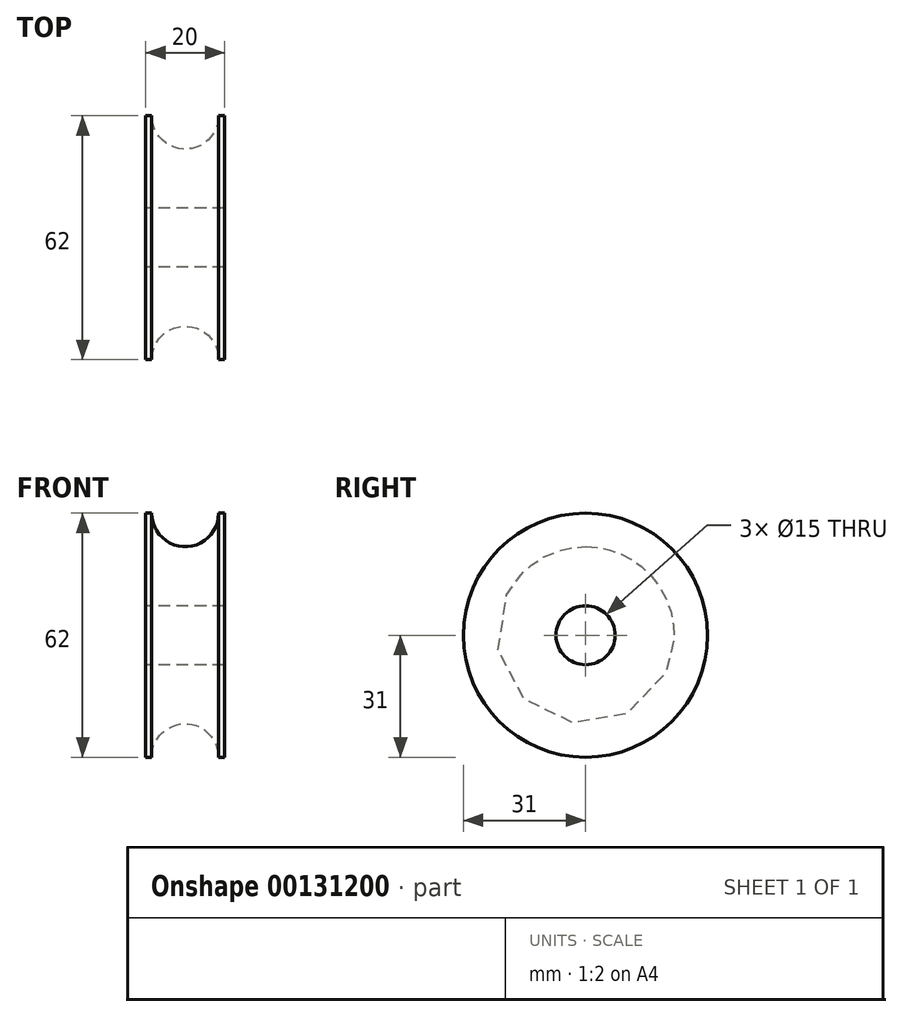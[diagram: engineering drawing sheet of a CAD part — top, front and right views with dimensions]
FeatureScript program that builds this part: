
annotation { "Feature Type Name" : "Feature", "Feature Type Description" : "" }
export const myFeature = defineFeature(function(context is Context, id is Id, definition is map)
    precondition{}
    {
        {
            var Q0;
            Q0=qCreatedBy(makeId("Front.planeOp"),FACE);
            var sketch = newSketch(context, id + "F0", { "sketchPlane" : qUnion([Q0])});
            skLineSegment(sketch, "E0", {"start": v(0, 0) * mm, "end": v(29.21, 0) * mm});
            skLineSegment(sketch, "E1", {"start": v(-10, 7.5) * mm, "end": v(10, 7.5) * mm});
            skLineSegment(sketch, "E2", {"start": v(10, 7.5) * mm, "end": v(10, 31) * mm});
            skLineSegment(sketch, "E3", {"start": v(10, 31) * mm, "end": v(8.5, 31) * mm});
            skLineSegment(sketch, "E4", {"start": v(-10, 31) * mm, "end": v(-10, 7.5) * mm});
            skLineSegment(sketch, "E5", {"start": v(0, 0) * mm, "end": v(0, 7.5) * mm});
            skArc(sketch, "E6", {"start": v(-8.5, 31) * mm, "mid": v(0, 22.5) * mm, "end": v(8.5, 31) * mm});
            skLineSegment(sketch, "E7.trimOffspring", {"start": v(-8.5, 31) * mm, "end": v(-10, 31) * mm});
            skSolve(sketch);
        }
        {
            var Q0;
            {var subQ0=sQuery(id+"F0.wireOp",EDGE,"E2");Q0=makeQuery(id+"F0.imprint","IMPRINT",FACE,{"disambiguationData":[TD([[makeQuery(id+"F0.imprint","IMPRINT",EDGE,{"derivedFrom":subQ0}),1.0]])]});}
            var Q1;
            Q1=sQuery(id+"F0.wireOp",EDGE,"E0");
            revolve(context, id + "F1", {"entities" : qUnion([Q0]), "axis" : qUnion([Q1]), "revolveType" : RevolveType.FULL});
        }
    });
